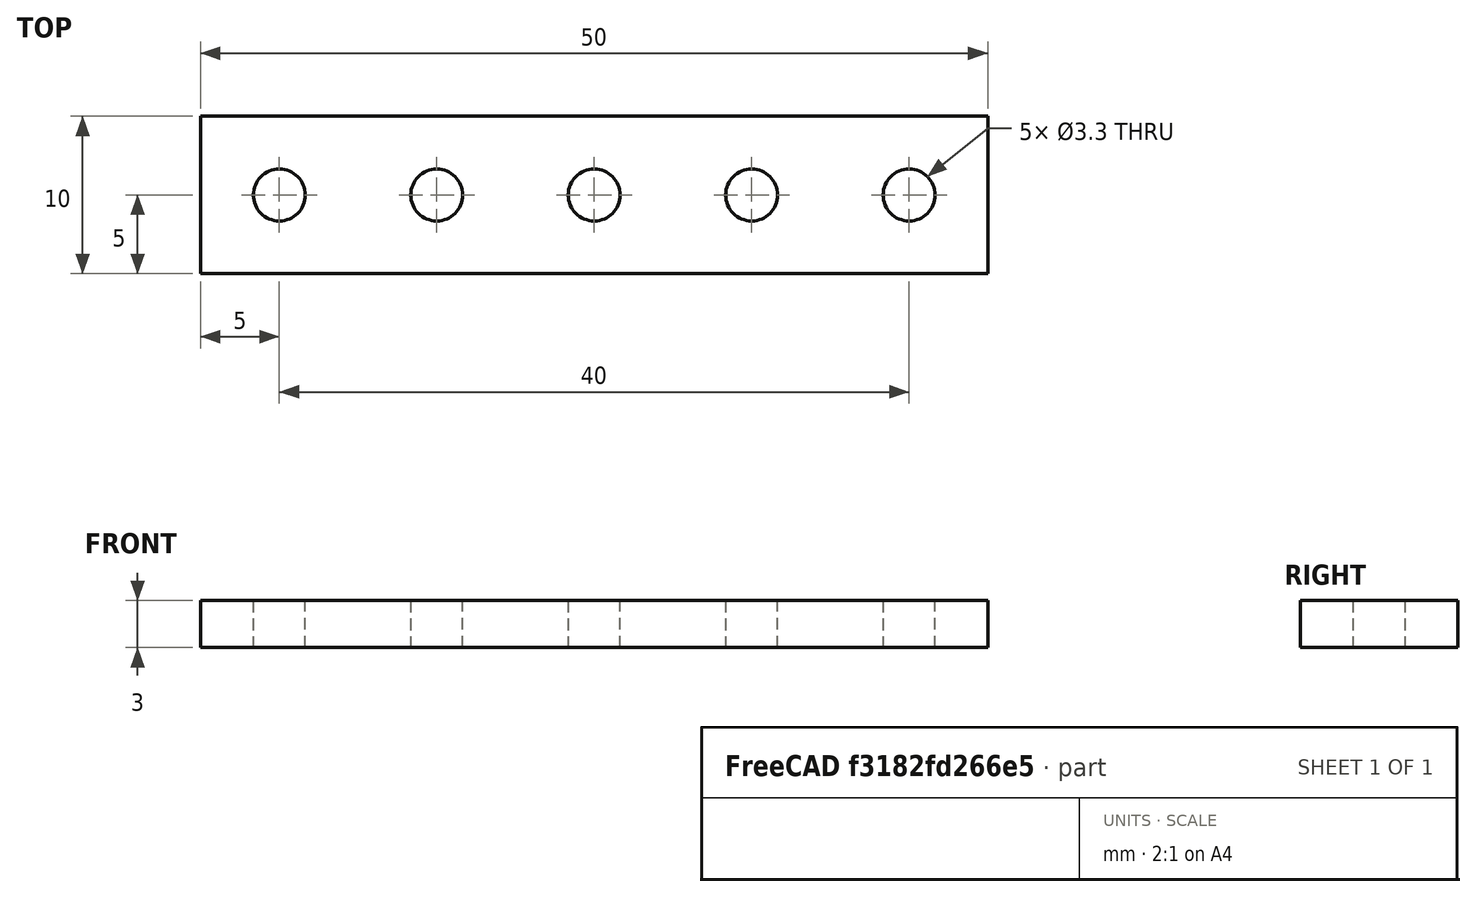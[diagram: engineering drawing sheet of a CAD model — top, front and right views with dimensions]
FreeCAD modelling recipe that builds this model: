
FCSTD DOCUMENT  (FreeCAD 0.21R33694 (Git))
Label: Solución Reto 3
License: All rights reserved
LicenseURL: http://en.wikipedia.org/wiki/All_rights_reserved
objects: Sketcher::SketchObject×1, PartDesign::Pad×1, PartDesign::Body×1
note: 4 computed .brp shape members not serialized (recipe doc carries the construction recipe); baked Part::Feature solids carry a one-line shape summary decoded from their .brp

FEATURE [Sketcher::SketchObject] Sketch
  FullyConstrained = true
  MapMode = 5
  Support = -> [XY_Plane]
  sketch-geometry (9):
    g0: Circle CenterX=0 CenterY=0 CenterZ=0 NormalX=0 NormalY=0 NormalZ=1 AngleXU=0 Radius=1.65
    g1: Circle CenterX=-20 CenterY=0 CenterZ=0 NormalX=0 NormalY=0 NormalZ=1 AngleXU=0 Radius=1.65
    g2: Circle CenterX=-10 CenterY=0 CenterZ=0 NormalX=0 NormalY=0 NormalZ=1 AngleXU=0 Radius=1.65
    g3: Circle CenterX=10 CenterY=0 CenterZ=0 NormalX=0 NormalY=0 NormalZ=1 AngleXU=0 Radius=1.65
    g4: Circle CenterX=20 CenterY=0 CenterZ=0 NormalX=0 NormalY=0 NormalZ=1 AngleXU=0 Radius=1.65
    g5: LineSegment StartX=-25 StartY=5 StartZ=0 EndX=25 EndY=5 EndZ=0
    g6: LineSegment StartX=25 StartY=5 StartZ=0 EndX=25 EndY=-5 EndZ=0
    g7: LineSegment StartX=25 StartY=-5 StartZ=0 EndX=-25 EndY=-5 EndZ=0
    g8: LineSegment StartX=-25 StartY=-5 StartZ=0 EndX=-25 EndY=5 EndZ=0
  constraints (22):
    c: Coincident(g0,g-1)
    c: Diameter(g0) = 3.3
    c: Equal(g0, g1-g4) x4
    c: PointOnObject(g1,g-1)
    c: PointOnObject(g2,g-1)
    c: PointOnObject(g3,g-1)
    c: PointOnObject(g4,g-1)
    c: Distance(g1,g2) = 10
    c: Distance(g2,g0) = 10
    c: Distance(g3,g4) = 10
    c: Distance(g0,g3) = 10
    c: Coincident(g5,g6)
    c: Coincident(g6,g7)
    c: Coincident(g7,g8)
    c: Coincident(g8,g5)
    c: Horizontal(g5)
    c: Horizontal(g7)
    c: Vertical(g6)
    c: Vertical(g8)
    c: DistanceX(g7,g7) = 50
    c: DistanceY(g6,g6) = 10
    c: Symmetric(g5,g6,g0)
FEATURE [PartDesign::Pad] Pad
  Direction = (0,0,1)
  Length = 3
  Length2 = 10
  Profile = -> Sketch
  ReferenceAxis = -> Sketch [N_Axis]
  Refine = true
  Type = 0
FEATURE [PartDesign::Body] Body  label="Cuerpo"
  Group = -> [Sketch,Pad]
  Origin = -> Origin
  Tip = -> Pad
